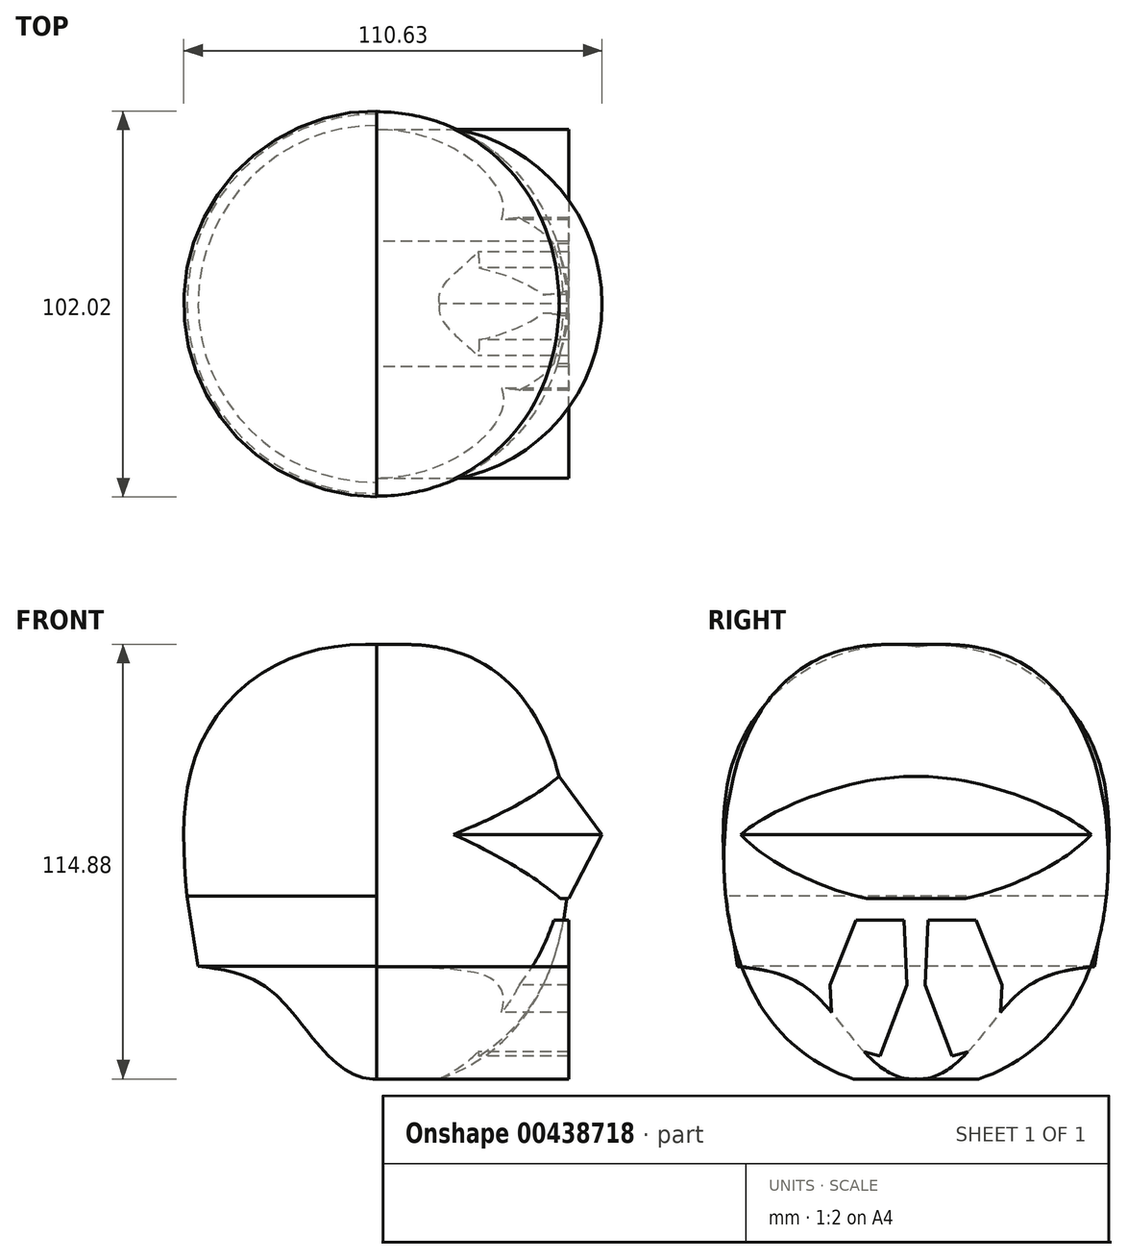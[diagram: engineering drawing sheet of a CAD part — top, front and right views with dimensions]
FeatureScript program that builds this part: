
annotation { "Feature Type Name" : "Feature", "Feature Type Description" : "" }
export const myFeature = defineFeature(function(context is Context, id is Id, definition is map)
    precondition{}
    {
        {
            var Q0;
            Q0=qCreatedBy(makeId("Front.planeOp"),FACE);
            var sketch = newSketch(context, id + "F0", { "sketchPlane" : qUnion([Q0])});
            skLineSegment(sketch, "E0", {"start": v(0, 65.97) * mm, "end": v(0, -48.33) * mm});
            skPoint(sketch, "E1", {"position": v(0, 8.82) * mm});
            skFitSpline(sketch, "E2", {"points": [v(0, 65.97) * mm, v(50.8, 10.3) * mm, v(16.55, -48.33) * mm], "startDerivative": vector(225.56, 30.07) * mm, "endDerivative": vector(-147.36, -49.12) * mm});
            skLineSegment(sketch, "E3", {"start": v(16.55, -48.33) * mm, "end": v(0, -48.33) * mm});
            skPoint(sketch, "E4", {"position": v(50.33, 0) * mm});
            skLineSegment(sketch, "E5", {"start": v(0, 0) * mm, "end": v(50.33, 0) * mm});
            skLineSegment(sketch, "E6", {"start": v(16.55, 65.73) * mm, "end": v(16.55, -48.33) * mm});
            skSolve(sketch);
        }
        {
            var Q0;
            Q0 = qSketchRegion(id + "F0", true);
            var Q1;
            Q1=sQuery(id+"F0.wireOp",EDGE,"E0");
            revolve(context, id + "F1", {"entities" : qUnion([Q0]), "axis" : qUnion([Q1]), "revolveType" : RevolveType.SYMMETRIC, "angle" : 180 * degree});
        }
        {
            var Q0;
            Q0=qCreatedBy(makeId("Front.planeOp"),FACE);
            var sketch = newSketch(context, id + "F2", { "sketchPlane" : qUnion([Q0])});
            skLineSegment(sketch, "E7", {"start": v(-50.17, 0) * mm, "end": v(-47.18, -18.6) * mm});
            skFitSpline(sketch, "E8", {"points": [v(-47.18, -18.6) * mm, v(-25.93, -26.77) * mm, v(0, -48.28) * mm], "startDerivative": vector(54.4, -6.04) * mm, "endDerivative": vector(59.2, 5.5) * mm});
            skLineSegment(sketch, "E9", {"start": v(0, 66.48) * mm, "end": v(0, -48.28) * mm});
            skFitSpline(sketch, "E10", {"points": [v(0, 66.48) * mm, v(-43.9, 45.18) * mm, v(-50.17, 0) * mm], "startDerivative": vector(-128.5, 5.95) * mm, "endDerivative": vector(11.2, -121.67) * mm});
            skSolve(sketch);
        }
        {
            var Q0;
            Q0=makeQuery(id+"F2.imprint","IMPRINT",FACE,{"disambiguationData":[TD([[makeQuery(id+"F2.imprint","IMPRINT",EDGE,{"derivedFrom":sQuery(id+"F2.wireOp",EDGE,"E7")}),1.0]])]});
            var Q1;
            Q1=sQuery(id+"F2.wireOp",EDGE,"E9");
            revolve(context, id + "F3", {"operationType" : NewBodyOperationType.ADD, "entities" : qUnion([Q0]), "axis" : qUnion([Q1]), "revolveType" : RevolveType.SYMMETRIC, "angle" : 180 * degree});
        }
        {
            var Q0;
            Q0=qCreatedBy(makeId("Front.planeOp"),FACE);
            var sketch = newSketch(context, id + "F4", { "sketchPlane" : qUnion([Q0])});
            skPoint(sketch, "E11", {"position": v(50.84, -0.6) * mm});
            skPoint(sketch, "E12", {"position": v(48.29, 31.6) * mm});
            skLineSegment(sketch, "E13", {"start": v(48.29, 31.6) * mm, "end": v(59.63, 16.3) * mm});
            skLineSegment(sketch, "E14", {"start": v(59.63, 16.3) * mm, "end": v(50.84, -0.6) * mm});
            skPoint(sketch, "E15", {"position": v(12.7, 16.3) * mm});
            skPoint(sketch, "E16", {"position": v(12.7, 65.95) * mm});
            skPoint(sketch, "E17", {"position": v(12.7, -47.92) * mm});
            skLineSegment(sketch, "E18", {"start": v(12.7, -47.92) * mm, "end": v(12.7, 65.95) * mm});
            skLineSegment(sketch, "E19", {"start": v(48.29, 31.6) * mm, "end": v(12.7, 16.3) * mm});
            skLineSegment(sketch, "E20", {"start": v(12.7, 16.3) * mm, "end": v(50.84, -0.6) * mm});
            skPoint(sketch, "E21", {"position": v(0, 66) * mm});
            skSolve(sketch);
        }
        {
            var Q0;
            Q0=makeQuery(id+"F4.imprint","IMPRINT",FACE,{"disambiguationData":[TD([[makeQuery(id+"F4.imprint","IMPRINT",EDGE,{"derivedFrom":sQuery(id+"F4.wireOp",EDGE,"E13")}),-1.0]])]});
            var Q1;
            Q1=sQuery(id+"F4.wireOp",EDGE,"E18");
            revolve(context, id + "F5", {"operationType" : NewBodyOperationType.ADD, "entities" : qUnion([Q0]), "axis" : qUnion([Q1]), "revolveType" : RevolveType.SYMMETRIC, "angle" : 180 * degree});
        }
        {
            var Q0;
            Q0=qCreatedBy(makeId("Right.planeOp"),FACE);
            var sketch = newSketch(context, id + "F6", { "sketchPlane" : qUnion([Q0])});
            skPoint(sketch, "E22", {"position": v(0, 0) * mm});
            skPoint(sketch, "E23", {"position": v(0, -6.35) * mm});
            skPoint(sketch, "E24", {"position": v(-3.18, -6.35) * mm});
            skPoint(sketch, "E25", {"position": v(3.18, -6.35) * mm});
            skPoint(sketch, "E26", {"position": v(-15.88, -6.35) * mm});
            skPoint(sketch, "E27", {"position": v(15.88, -6.35) * mm});
            skPoint(sketch, "E28", {"position": v(0, -48.58) * mm});
            skPoint(sketch, "E29", {"position": v(-12.7, -48.58) * mm});
            skPoint(sketch, "E30", {"position": v(12.7, -48.58) * mm});
            skPoint(sketch, "E31", {"position": v(0, -42.23) * mm});
            skPoint(sketch, "E32", {"position": v(-9.53, -42.23) * mm});
            skPoint(sketch, "E33", {"position": v(9.53, -42.23) * mm});
            skPoint(sketch, "E34", {"position": v(-9.52, -6.35) * mm});
            skPoint(sketch, "E35", {"position": v(9.52, -6.35) * mm});
            skPoint(sketch, "E36", {"position": v(21.82, -39.05) * mm});
            skPoint(sketch, "E37", {"position": v(-21.82, -39.05) * mm});
            skLineSegment(sketch, "E38", {"start": v(-21.82, -39.05) * mm, "end": v(-9.52, -42.23) * mm});
            skLineSegment(sketch, "E39", {"start": v(9.53, -42.23) * mm, "end": v(21.82, -39.05) * mm});
            skPoint(sketch, "E40", {"position": v(-15.67, -40.64) * mm});
            skPoint(sketch, "E41", {"position": v(15.67, -40.64) * mm});
            skLineSegment(sketch, "E42", {"start": v(-9.52, -6.35) * mm, "end": v(-15.67, -40.64) * mm});
            skLineSegment(sketch, "E43", {"start": v(9.53, -6.35) * mm, "end": v(15.67, -40.64) * mm});
            skPoint(sketch, "E44", {"position": v(-12.6, -23.5) * mm});
            skPoint(sketch, "E45", {"position": v(12.6, -23.5) * mm});
            skPoint(sketch, "E46", {"position": v(-22.76, -23.5) * mm});
            skPoint(sketch, "E47", {"position": v(-2.44, -23.5) * mm});
            skPoint(sketch, "E48", {"position": v(2.44, -23.5) * mm});
            skPoint(sketch, "E49", {"position": v(22.76, -23.5) * mm});
            skLineSegment(sketch, "E50", {"start": v(3.18, -6.35) * mm, "end": v(2.44, -23.5) * mm});
            skLineSegment(sketch, "E51", {"start": v(2.44, -23.5) * mm, "end": v(9.53, -42.23) * mm});
            skLineSegment(sketch, "E52", {"start": v(15.88, -6.35) * mm, "end": v(22.76, -23.5) * mm});
            skLineSegment(sketch, "E53", {"start": v(21.82, -39.05) * mm, "end": v(22.76, -23.5) * mm});
            skLineSegment(sketch, "E54", {"start": v(-2.44, -23.5) * mm, "end": v(-3.18, -6.35) * mm});
            skLineSegment(sketch, "E55", {"start": v(-2.44, -23.5) * mm, "end": v(-9.53, -42.23) * mm});
            skLineSegment(sketch, "E56", {"start": v(-21.82, -39.05) * mm, "end": v(-22.76, -23.5) * mm});
            skLineSegment(sketch, "E57", {"start": v(-15.88, -6.35) * mm, "end": v(-22.76, -23.5) * mm});
            skLineSegment(sketch, "E58", {"start": v(-9.52, -6.35) * mm, "end": v(-3.18, -6.35) * mm});
            skLineSegment(sketch, "E59", {"start": v(3.18, -6.35) * mm, "end": v(9.52, -6.35) * mm});
            skLineSegment(sketch, "E60", {"start": v(-9.52, -6.35) * mm, "end": v(-15.88, -6.35) * mm});
            skLineSegment(sketch, "E61", {"start": v(9.52, -6.35) * mm, "end": v(15.88, -6.35) * mm});
            skLineSegment(sketch, "E62", {"start": v(-22.76, -23.5) * mm, "end": v(-2.44, -23.5) * mm});
            skLineSegment(sketch, "E63", {"start": v(2.44, -23.5) * mm, "end": v(22.76, -23.5) * mm});
            skSolve(sketch);
        }
        {
            var Q0;
            {var subQ0=sQuery(id+"F6.wireOp",EDGE,"E51");Q0=makeQuery(id+"F6.imprint","IMPRINT",FACE,{"disambiguationData":[TD([[makeQuery(id+"F6.imprint","IMPRINT",EDGE,{"derivedFrom":subQ0}),1.0]])]});}
            var Q1;
            {var subQ0=sQuery(id+"F6.wireOp",EDGE,"E53");Q1=makeQuery(id+"F6.imprint","IMPRINT",FACE,{"disambiguationData":[TD([[makeQuery(id+"F6.imprint","IMPRINT",EDGE,{"derivedFrom":subQ0}),1.0]])]});}
            var Q2;
            {var subQ4=sQuery(id+"F6.wireOp",EDGE,"E54");Q2=makeQuery(id+"F6.imprint","IMPRINT",FACE,{"disambiguationData":[TD([[makeQuery(id+"F6.imprint","IMPRINT",EDGE,{"derivedFrom":subQ4}),1.0]])]});}
            var Q3;
            {var subQ4=sQuery(id+"F6.wireOp",EDGE,"E57");Q3=makeQuery(id+"F6.imprint","IMPRINT",FACE,{"disambiguationData":[TD([[makeQuery(id+"F6.imprint","IMPRINT",EDGE,{"derivedFrom":subQ4}),1.0]])]});}
            var Q4;
            {var subQ4=sQuery(id+"F6.wireOp",EDGE,"E50");Q4=makeQuery(id+"F6.imprint","IMPRINT",FACE,{"disambiguationData":[TD([[makeQuery(id+"F6.imprint","IMPRINT",EDGE,{"derivedFrom":subQ4}),1.0]])]});}
            var Q5;
            {var subQ4=sQuery(id+"F6.wireOp",EDGE,"E52");Q5=makeQuery(id+"F6.imprint","IMPRINT",FACE,{"disambiguationData":[TD([[makeQuery(id+"F6.imprint","IMPRINT",EDGE,{"derivedFrom":subQ4}),-1.0]])]});}
            var Q6;
            {var subQ0=sQuery(id+"F6.wireOp",EDGE,"E56");Q6=makeQuery(id+"F6.imprint","IMPRINT",FACE,{"disambiguationData":[TD([[makeQuery(id+"F6.imprint","IMPRINT",EDGE,{"derivedFrom":subQ0}),-1.0]])]});}
            var Q7;
            {var subQ0=sQuery(id+"F6.wireOp",EDGE,"E55");Q7=makeQuery(id+"F6.imprint","IMPRINT",FACE,{"disambiguationData":[TD([[makeQuery(id+"F6.imprint","IMPRINT",EDGE,{"derivedFrom":subQ0}),-1.0]])]});}
            var Q8;
            {var subQ0=sQuery(id+"F0.wireOp",EDGE,"E3");var subQ1=makeQuery(id+"F1.opRevolve","CAP_FACE",FACE,{"disambiguationData":[OSD([sQuery(id+"F0.wireOp",EDGE,"E0"),sQuery(id+"F0.wireOp",EDGE,"E2"),subQ0])],"isStart":true});Q8=makeQuery(id+"F3.boolean.opBoolean","SPLIT",FACE,{"disambiguationData":[TD([subQ1,makeQuery(id+"F1.opRevolve","SWEPT_FACE",FACE,{"disambiguationData":[OSD([subQ0])]}),makeQuery(id+"F3.opRevolve","SWEPT_FACE",FACE,{"disambiguationData":[OSD([sQuery(id+"F2.wireOp",EDGE,"E8")])]})])],"derivedFrom":subQ1});}
            var Q9;
            Q9=makeQuery(id+"F1.opRevolve","SWEPT_FACE",FACE,{"disambiguationData":[OSD([sQuery(id+"F0.wireOp",EDGE,"E2")])]});
            extrude(context, id + "F7", {"entities" : qUnion([Q0, Q1, Q2, Q3, Q4, Q5, Q6, Q7, Q8]), "operationType" : NewBodyOperationType.ADD, "endBoundEntityFace" : qUnion([Q9]), "depth" : 50.8 * mm});
        }
    });
